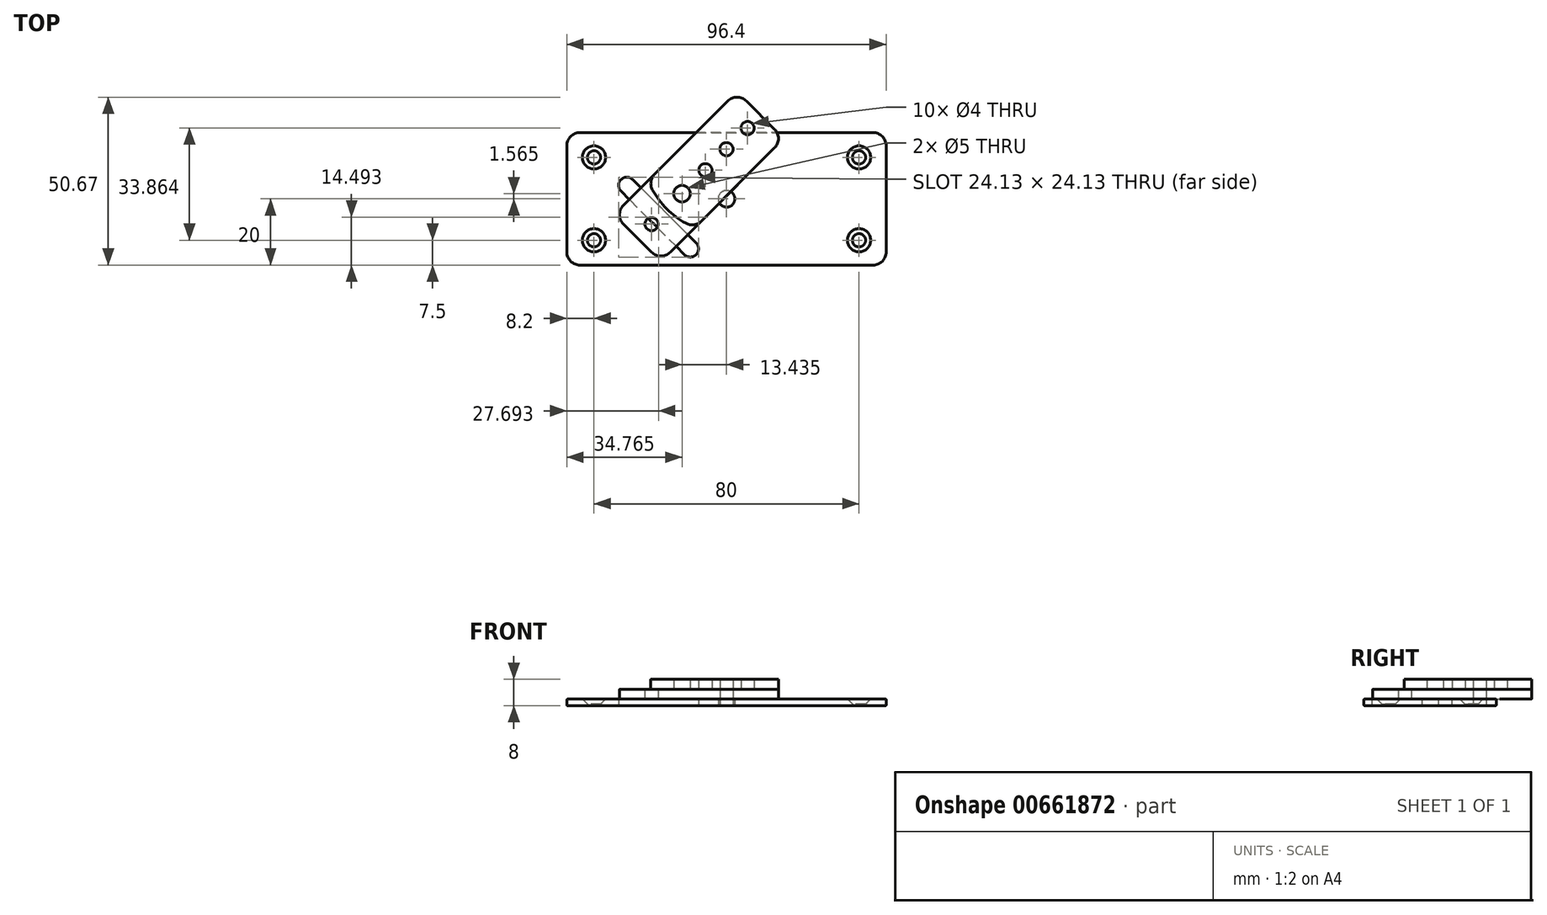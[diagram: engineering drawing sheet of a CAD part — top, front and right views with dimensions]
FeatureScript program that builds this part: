
annotation { "Feature Type Name" : "Feature", "Feature Type Description" : "" }
export const myFeature = defineFeature(function(context is Context, id is Id, definition is map)
    precondition{}
    {
        {
            var Q0;
            Q0=qCreatedBy(makeId("Front.planeOp"),FACE);
            var sketch = newSketch(context, id + "F0", { "sketchPlane" : qUnion([Q0])});
            skLineSegment(sketch, "E0", {"start": v(-48.2, 2) * mm, "end": v(48.2, 2) * mm});
            skLineSegment(sketch, "E1", {"start": v(48.2, 0) * mm, "end": v(-48.2, 0) * mm});
            skLineSegment(sketch, "E2", {"start": v(-48.2, 0) * mm, "end": v(-48.2, 2) * mm});
            skLineSegment(sketch, "E3", {"start": v(48.2, 2) * mm, "end": v(48.2, 0) * mm});
            skSolve(sketch);
        }
        {
            var Q0;
            Q0 = qSketchRegion(id + "F0", true);
            extrude(context, id + "F1", {"entities" : qUnion([Q0]), "depth" : 40 * mm, "offsetDistance" : 25 * mm, "symmetric" : true});
        }
        {
            var Q0;
            Q0=makeQuery(id+"F1.opExtrude","CAP_EDGE",EDGE,{"disambiguationData":[OSD([sQuery(id+"F0.wireOp",EDGE,"6336iILO-EXUb-a0q3-mLpg-2h5BAeNqFCQp")])],"isStart":false});
            var Q1;
            Q1=makeQuery(id+"F1.opExtrude","CAP_EDGE",EDGE,{"disambiguationData":[OSD([sQuery(id+"F0.wireOp",EDGE,"3FDj9TMQ-peiz-3DIO-RIDN-a6zGkZZwx6A8")])],"isStart":false});
            var Q2;
            Q2=makeQuery(id+"F1.opExtrude","CAP_EDGE",EDGE,{"disambiguationData":[OSD([sQuery(id+"F0.wireOp",EDGE,"3FDj9TMQ-peiz-3DIO-RIDN-a6zGkZZwx6A8")])],"isStart":true});
            var Q3;
            Q3=makeQuery(id+"F1.opExtrude","CAP_EDGE",EDGE,{"disambiguationData":[OSD([sQuery(id+"F0.wireOp",EDGE,"6336iILO-EXUb-a0q3-mLpg-2h5BAeNqFCQp")])],"isStart":true});
            var Q4;
            Q4=makeQuery(id+"F1.opExtrude","CAP_EDGE",EDGE,{"disambiguationData":[OSD([sQuery(id+"F0.wireOp",EDGE,"E2")])],"isStart":false});
            var Q5;
            Q5=makeQuery(id+"F1.opExtrude","CAP_EDGE",EDGE,{"disambiguationData":[OSD([sQuery(id+"F0.wireOp",EDGE,"E3")])],"isStart":false});
            var Q6;
            Q6=makeQuery(id+"F1.opExtrude","CAP_EDGE",EDGE,{"disambiguationData":[OSD([sQuery(id+"F0.wireOp",EDGE,"E3")])],"isStart":true});
            var Q7;
            Q7=makeQuery(id+"F1.opExtrude","CAP_EDGE",EDGE,{"disambiguationData":[OSD([sQuery(id+"F0.wireOp",EDGE,"E2")])],"isStart":true});
            fillet(context, id + "F2", {"entities" : qUnion([Q0, Q1, Q2, Q3, Q4, Q5, Q6, Q7]), "radius" : 4 * mm, "tangentPropagation" : true, "allowEdgeOverflow" : false});
        }
        {
            var Q0;
            Q0=makeQuery(id+"F1.opExtrude","SWEPT_FACE",FACE,{"disambiguationData":[OSD([sQuery(id+"F0.wireOp",EDGE,"E0")])]});
            var Q1;
            Q1=makeQuery(id+"F1.opExtrude","SWEPT_FACE",FACE,{"disambiguationData":[OSD([sQuery(id+"F0.wireOp",EDGE,"E1")])]});
            fillet(context, id + "F3", {"entities" : qUnion([Q0, Q1]), "radius" : 0.25 * mm, "tangentPropagation" : true, "allowEdgeOverflow" : false});
        }
        {
            var Q0;
            Q0=qCreatedBy(makeId("Top.planeOp"),FACE);
            var sketch = newSketch(context, id + "F4", { "sketchPlane" : qUnion([Q0])});
            skLineSegment(sketch, "E4.bottom", {"start": v(-48.2, 20) * mm, "end": v(48.2, 20) * mm, "construction": true});
            skLineSegment(sketch, "E4.top", {"start": v(-48.2, -20) * mm, "end": v(48.2, -20) * mm, "construction": true});
            skLineSegment(sketch, "E4.left", {"start": v(-48.2, 20) * mm, "end": v(-48.2, -20) * mm, "construction": true});
            skLineSegment(sketch, "E4.right", {"start": v(48.2, 20) * mm, "end": v(48.2, -20) * mm, "construction": true});
            skLineSegment(sketch, "E5", {"start": v(0, 20) * mm, "end": v(0, -20) * mm, "construction": true});
            skLineSegment(sketch, "E6.bottom", {"start": v(-40, 12.5) * mm, "end": v(40, 12.5) * mm, "construction": true});
            skLineSegment(sketch, "E6.top", {"start": v(-40, -12.5) * mm, "end": v(40, -12.5) * mm, "construction": true});
            skLineSegment(sketch, "E6.left", {"start": v(-40, 12.5) * mm, "end": v(-40, -12.5) * mm, "construction": true});
            skLineSegment(sketch, "E6.right", {"start": v(40, 12.5) * mm, "end": v(40, -12.5) * mm, "construction": true});
            skPoint(sketch, "E6.middle", {"position": v(0, 0) * mm});
            skCircle(sketch, "E7", {"center": v(-40, 12.5) * mm, "radius": 2 * mm});
            skCircle(sketch, "E8", {"center": v(-40, -12.5) * mm, "radius": 2 * mm});
            skCircle(sketch, "E9", {"center": v(40, 12.5) * mm, "radius": 2 * mm});
            skCircle(sketch, "E10", {"center": v(40, -12.5) * mm, "radius": 2 * mm});
            skCircle(sketch, "E11", {"center": v(0, 0) * mm, "radius": 2.5 * mm});
            skSolve(sketch);
        }
        {
            var Q0;
            Q0 = qSketchRegion(id + "F4", true);
            extrude(context, id + "F5", {"entities" : qUnion([Q0]), "operationType" : NewBodyOperationType.REMOVE, "endBound" : BoundingType.THROUGH_ALL, "depth" : 25 * mm, "offsetDistance" : 25 * mm});
        }
        {
            var Q0;
            Q0=makeQuery(id+"F5.boolean.opBoolean","INTERSECT",EDGE,{"derivedFrom":[makeQuery(id+"F1.opExtrude","SWEPT_FACE",FACE,{"disambiguationData":[OSD([sQuery(id+"F0.wireOp",EDGE,"E0")])]}),makeQuery(id+"F5.opExtrude","SWEPT_FACE",FACE,{"disambiguationData":[OSD([sQuery(id+"F4.wireOp",EDGE,"E7")])]})]});
            var Q1;
            Q1=makeQuery(id+"F5.boolean.opBoolean","INTERSECT",EDGE,{"derivedFrom":[makeQuery(id+"F1.opExtrude","SWEPT_FACE",FACE,{"disambiguationData":[OSD([sQuery(id+"F0.wireOp",EDGE,"E0")])]}),makeQuery(id+"F5.opExtrude","SWEPT_FACE",FACE,{"disambiguationData":[OSD([sQuery(id+"F4.wireOp",EDGE,"E8")])]})]});
            var Q2;
            Q2=makeQuery(id+"F5.boolean.opBoolean","INTERSECT",EDGE,{"derivedFrom":[makeQuery(id+"F1.opExtrude","SWEPT_FACE",FACE,{"disambiguationData":[OSD([sQuery(id+"F0.wireOp",EDGE,"E0")])]}),makeQuery(id+"F5.opExtrude","SWEPT_FACE",FACE,{"disambiguationData":[OSD([sQuery(id+"F4.wireOp",EDGE,"E10")])]})]});
            var Q3;
            Q3=makeQuery(id+"F5.boolean.opBoolean","INTERSECT",EDGE,{"derivedFrom":[makeQuery(id+"F1.opExtrude","SWEPT_FACE",FACE,{"disambiguationData":[OSD([sQuery(id+"F0.wireOp",EDGE,"E0")])]}),makeQuery(id+"F5.opExtrude","SWEPT_FACE",FACE,{"disambiguationData":[OSD([sQuery(id+"F4.wireOp",EDGE,"E9")])]})]});
            chamfer(context, id + "F6", {"entities" : qUnion([Q0, Q1, Q2, Q3]), "width" : 1.5 * mm, "tangentPropagation" : true});
        }
        {
            var Q0;
            Q0=qCreatedBy(makeId("Top.planeOp"),FACE);
            var sketch = newSketch(context, id + "F7", { "sketchPlane" : qUnion([Q0])});
            skCircle(sketch, "E12", {"center": v(0, 15) * mm, "radius": 2 * mm});
            skLineSegment(sketch, "E13", {"start": v(0, 15) * mm, "end": v(-10.94, -15.07) * mm, "construction": true});
            skLineSegment(sketch, "E14", {"start": v(0, 15) * mm, "end": v(0, 0) * mm});
            skLineSegment(sketch, "E15", {"start": v(0, 15) * mm, "end": v(-30.07, 4.06) * mm, "construction": true});
            skArc(sketch, "E16", {"start": v(-30.07, 4.06) * mm, "mid": v(-22.63, -7.63) * mm, "end": v(-10.94, -15.07) * mm, "construction": true});
            skLineSegment(sketch, "E17", {"start": v(0, 15) * mm, "end": v(-22.63, -7.63) * mm, "construction": true});
            skLineSegment(sketch, "E18", {"start": v(-7.07, 22.07) * mm, "end": v(7.07, 7.93) * mm, "construction": true});
            skLineSegment(sketch, "E19", {"start": v(-33.94, -4.8) * mm, "end": v(3.18, 32.32) * mm, "construction": true});
            skLineSegment(sketch, "E20", {"start": v(3.18, 32.32) * mm, "end": v(17.32, 18.18) * mm, "construction": true});
            skLineSegment(sketch, "E21", {"start": v(17.32, 18.18) * mm, "end": v(-19.8, -18.94) * mm, "construction": true});
            skLineSegment(sketch, "E22", {"start": v(-19.8, -18.94) * mm, "end": v(-33.94, -4.8) * mm, "construction": true});
            skCircle(sketch, "E23", {"center": v(-6.36, 8.64) * mm, "radius": 2 * mm, "construction": true});
            skCircle(sketch, "E24.MirrorC", {"center": v(6.36, 21.36) * mm, "radius": 2 * mm, "construction": true});
            skCircle(sketch, "E25", {"center": v(-22.63, -7.63) * mm, "radius": 2 * mm, "construction": true});
            skCircle(sketch, "E26", {"center": v(-13.44, 1.56) * mm, "radius": 2 * mm, "construction": true});
            skLineSegment(sketch, "E27", {"start": v(-17.32, 11.82) * mm, "end": v(-3.18, -2.32) * mm, "construction": true});
            skCircle(sketch, "E28", {"center": v(-13.44, 1.56) * mm, "radius": 4 * mm, "construction": true});
            skArc(sketch, "E29", {"start": v(-22.24, 6.9) * mm, "mid": v(-17.68, -2.68) * mm, "end": v(-8.1, -7.24) * mm, "construction": true});
            skCircle(sketch, "E30", {"center": v(-22.63, -7.63) * mm, "radius": 4.5 * mm, "construction": true});
            skLineSegment(sketch, "E31", {"start": v(-28.3, 5.82) * mm, "end": v(-9.18, -13.3) * mm});
            skArc(sketch, "E32", {"start": v(-28.3, 5.82) * mm, "mid": v(-31.84, 5.82) * mm, "end": v(-31.84, 2.29) * mm});
            skArc(sketch, "E33", {"start": v(-12.71, -16.84) * mm, "mid": v(-9.18, -16.84) * mm, "end": v(-9.18, -13.3) * mm});
            skLineSegment(sketch, "E34", {"start": v(-31.84, 2.29) * mm, "end": v(-12.71, -16.84) * mm});
            skLineSegment(sketch, "E35", {"start": v(-30.07, 4.06) * mm, "end": v(-10.94, -15.07) * mm, "construction": true});
            skCircle(sketch, "E36", {"center": v(-20.5, -5.5) * mm, "radius": 2 * mm, "construction": true});
            skCircle(sketch, "E37", {"center": v(-20.5, -5.5) * mm, "radius": 4.5 * mm, "construction": true});
            skSolve(sketch);
        }
        {
            var Q0;
            Q0 = qSketchRegion(id + "F7", true);
            extrude(context, id + "F8", {"entities" : qUnion([Q0]), "operationType" : NewBodyOperationType.REMOVE, "endBound" : BoundingType.THROUGH_ALL, "depth" : 25 * mm, "offsetDistance" : 25 * mm});
        }
        {
            var Q0;
            Q0=makeQuery(id+"F1.opExtrude","SWEPT_FACE",FACE,{"disambiguationData":[OSD([sQuery(id+"F0.wireOp",EDGE,"E0")])]});
            var sketch = newSketch(context, id + "F9", { "sketchPlane" : qUnion([Q0])});
            skLineSegment(sketch, "E38.0", {"start": v(-31.11, -1.97) * mm, "end": v(0.35, 29.5) * mm});
            skLineSegment(sketch, "E38.1", {"start": v(6.01, 29.5) * mm, "end": v(14.5, 21.01) * mm});
            skLineSegment(sketch, "E38.2", {"start": v(14.5, 15.35) * mm, "end": v(-16.97, -16.11) * mm});
            skLineSegment(sketch, "E38.3", {"start": v(-22.63, -16.11) * mm, "end": v(-31.11, -7.63) * mm});
            skCircle(sketch, "E38.4", {"center": v(-22.63, -7.63) * mm, "radius": 2 * mm});
            skCircle(sketch, "E38.5", {"center": v(0, 15) * mm, "radius": 2 * mm});
            skPoint(sketch, "E39.visualSharp", {"position": v(3.18, 32.32) * mm});
            skArc(sketch, "E39.filletArc", {"start": v(6.01, 29.5) * mm, "mid": v(3.18, 30.67) * mm, "end": v(0.35, 29.5) * mm});
            skPoint(sketch, "E40.visualSharp", {"position": v(17.32, 18.18) * mm});
            skArc(sketch, "E40.filletArc", {"start": v(14.5, 15.35) * mm, "mid": v(15.67, 18.18) * mm, "end": v(14.5, 21.01) * mm});
            skPoint(sketch, "E41.visualSharp", {"position": v(-19.8, -18.94) * mm});
            skArc(sketch, "E41.filletArc", {"start": v(-22.63, -16.11) * mm, "mid": v(-19.8, -17.28) * mm, "end": v(-16.97, -16.11) * mm});
            skPoint(sketch, "E42.visualSharp", {"position": v(-33.94, -4.8) * mm});
            skArc(sketch, "E42.filletArc", {"start": v(-31.11, -1.97) * mm, "mid": v(-32.28, -4.8) * mm, "end": v(-31.11, -7.63) * mm});
            skSolve(sketch);
        }
        {
            var Q0;
            Q0 = qSketchRegion(id + "F9", true);
            extrude(context, id + "F10", {"entities" : qUnion([Q0]), "depth" : 3 * mm, "offsetDistance" : 25 * mm});
        }
        {
            var Q0;
            Q0=makeQuery(id+"F10.opExtrude","CAP_FACE",FACE,{"disambiguationData":[OSD([sQuery(id+"F9.wireOp",EDGE,"E38.0"),sQuery(id+"F9.wireOp",EDGE,"E38.1"),sQuery(id+"F9.wireOp",EDGE,"E38.2"),sQuery(id+"F9.wireOp",EDGE,"E38.3"),sQuery(id+"F9.wireOp",EDGE,"E38.4"),sQuery(id+"F9.wireOp",EDGE,"E38.5"),sQuery(id+"F9.wireOp",EDGE,"E39.filletArc"),sQuery(id+"F9.wireOp",EDGE,"E40.filletArc"),sQuery(id+"F9.wireOp",EDGE,"E41.filletArc"),sQuery(id+"F9.wireOp",EDGE,"E42.filletArc")])],"isStart":false});
            var sketch = newSketch(context, id + "F11", { "sketchPlane" : qUnion([Q0])});
            skCircle(sketch, "E43.0", {"center": v(6.36, 21.36) * mm, "radius": 2 * mm});
            skCircle(sketch, "E43.1", {"center": v(0, 15) * mm, "radius": 2 * mm});
            skCircle(sketch, "E43.2", {"center": v(-6.36, 8.64) * mm, "radius": 2 * mm});
            skLineSegment(sketch, "E43.3", {"start": v(-21.67, 7.47) * mm, "end": v(0.35, 29.5) * mm});
            skLineSegment(sketch, "E43.4", {"start": v(6.01, 29.5) * mm, "end": v(14.5, 21.01) * mm});
            skLineSegment(sketch, "E43.5", {"start": v(14.5, 15.35) * mm, "end": v(-7.53, -6.67) * mm});
            skCircle(sketch, "E44", {"center": v(-13.44, 1.56) * mm, "radius": 2.5 * mm});
            skArc(sketch, "E45", {"start": v(-22.35, 2.72) * mm, "mid": v(-18.03, -3.03) * mm, "end": v(-12.28, -7.35) * mm});
            skPoint(sketch, "E46.visualSharp", {"position": v(3.18, 32.32) * mm});
            skArc(sketch, "E46.filletArc", {"start": v(6.01, 29.5) * mm, "mid": v(3.18, 30.67) * mm, "end": v(0.35, 29.5) * mm});
            skPoint(sketch, "E47.visualSharp", {"position": v(17.32, 18.18) * mm});
            skArc(sketch, "E47.filletArc", {"start": v(14.5, 15.35) * mm, "mid": v(15.67, 18.18) * mm, "end": v(14.5, 21.01) * mm});
            skPoint(sketch, "E48.visualSharp", {"position": v(-23.66, 5.48) * mm});
            skArc(sketch, "E48.filletArc", {"start": v(-21.67, 7.47) * mm, "mid": v(-22.8, 5.2) * mm, "end": v(-22.35, 2.72) * mm});
            skPoint(sketch, "E49.visualSharp", {"position": v(-9.52, -8.66) * mm});
            skArc(sketch, "E49.filletArc", {"start": v(-12.28, -7.35) * mm, "mid": v(-9.8, -7.8) * mm, "end": v(-7.53, -6.67) * mm});
            skSolve(sketch);
        }
        {
            var Q0;
            Q0 = qSketchRegion(id + "F11", true);
            extrude(context, id + "F12", {"entities" : qUnion([Q0]), "depth" : 3 * mm, "offsetDistance" : 25 * mm});
        }
    });
